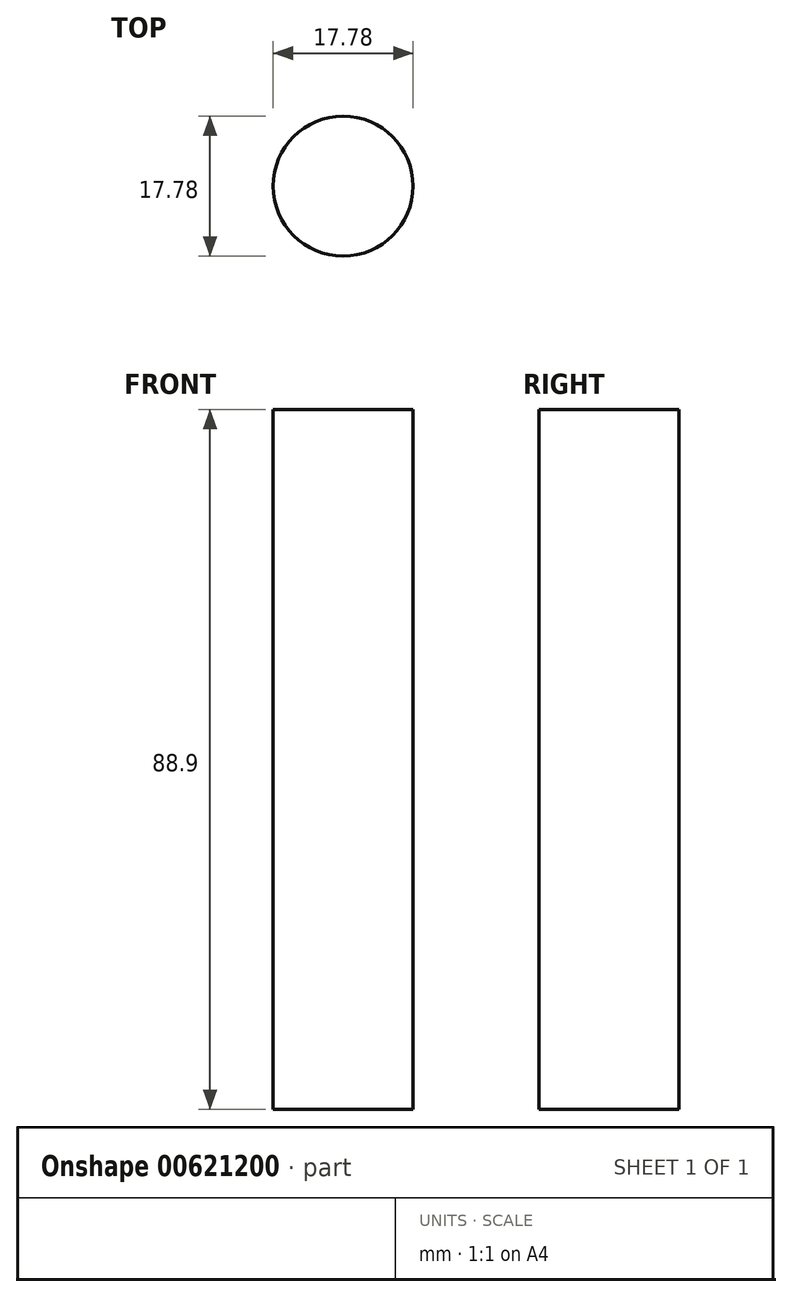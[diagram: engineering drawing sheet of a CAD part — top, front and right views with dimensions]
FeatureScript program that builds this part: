
annotation { "Feature Type Name" : "Feature", "Feature Type Description" : "" }
export const myFeature = defineFeature(function(context is Context, id is Id, definition is map)
    precondition{}
    {
        {
            var Q0;
            Q0=qCreatedBy(makeId("Top.planeOp"),FACE);
            var sketch = newSketch(context, id + "F0", { "sketchPlane" : qUnion([Q0])});
            skCircle(sketch, "E0", {"center": v(0, 0) * mm, "radius": 8.9 * mm});
            skSolve(sketch);
        }
        {
            var Q0;
            Q0=makeQuery(id+"F0.imprint","IMPRINT",FACE,{"disambiguationData":[TD([[makeQuery(id+"F0.imprint","IMPRINT",EDGE,{"derivedFrom":sQuery(id+"F0.wireOp",EDGE,"E0")}),1.0]])]});
            extrude(context, id + "F1", {"entities" : qUnion([Q0]), "depth" : 88.9 * mm, "offsetDistance" : 25.4 * mm});
        }
    });
